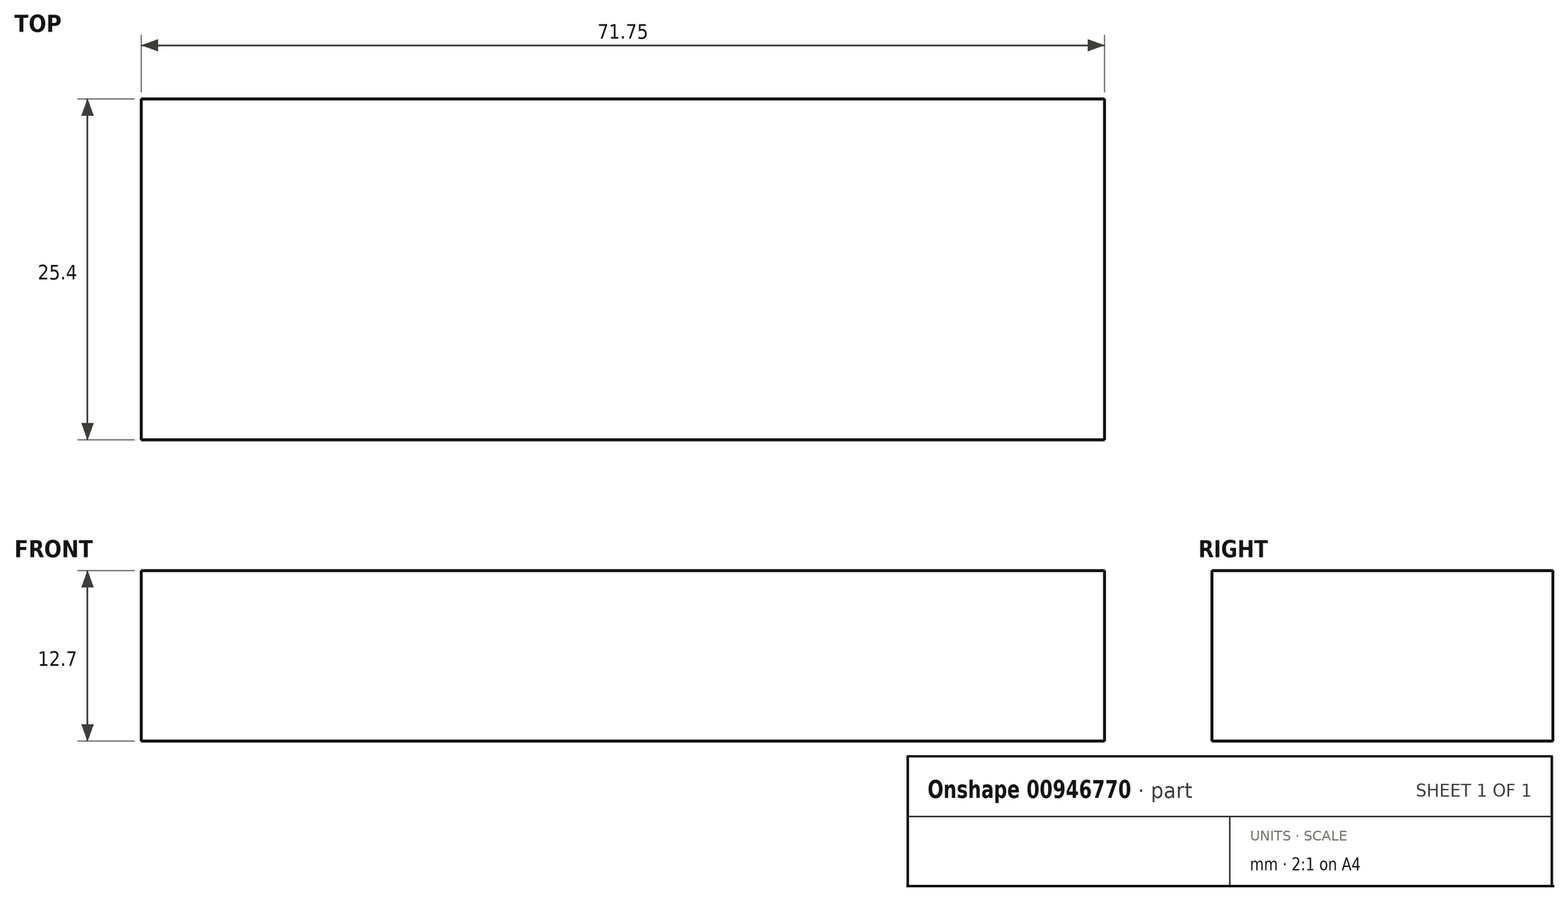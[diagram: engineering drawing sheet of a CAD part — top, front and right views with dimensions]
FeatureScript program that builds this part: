
annotation { "Feature Type Name" : "Feature", "Feature Type Description" : "" }
export const myFeature = defineFeature(function(context is Context, id is Id, definition is map)
    precondition{}
    {
        {
            var Q0;
            Q0=qCreatedBy(makeId("Right.planeOp"),FACE);
            var sketch = newSketch(context, id + "F0", { "sketchPlane" : qUnion([Q0])});
            skLineSegment(sketch, "E0.bottom", {"start": v(0, 0) * mm, "end": v(25.4, 0) * mm});
            skLineSegment(sketch, "E0.top", {"start": v(0, -12.7) * mm, "end": v(25.4, -12.7) * mm});
            skLineSegment(sketch, "E0.left", {"start": v(0, 0) * mm, "end": v(0, -12.7) * mm});
            skLineSegment(sketch, "E0.right", {"start": v(25.4, 0) * mm, "end": v(25.4, -12.7) * mm});
            skSolve(sketch);
        }
        {
            var Q0;
            Q0=makeQuery(id+"F0.imprint","IMPRINT",FACE,{"disambiguationData":[TD([[makeQuery(id+"F0.imprint","IMPRINT",EDGE,{"derivedFrom":sQuery(id+"F0.wireOp",EDGE,"E0.bottom")}),-1.0]])]});
            extrude(context, id + "F1", {"entities" : qUnion([Q0]), "depth" : 71.75 * mm, "offsetDistance" : 25.4 * mm});
        }
    });
